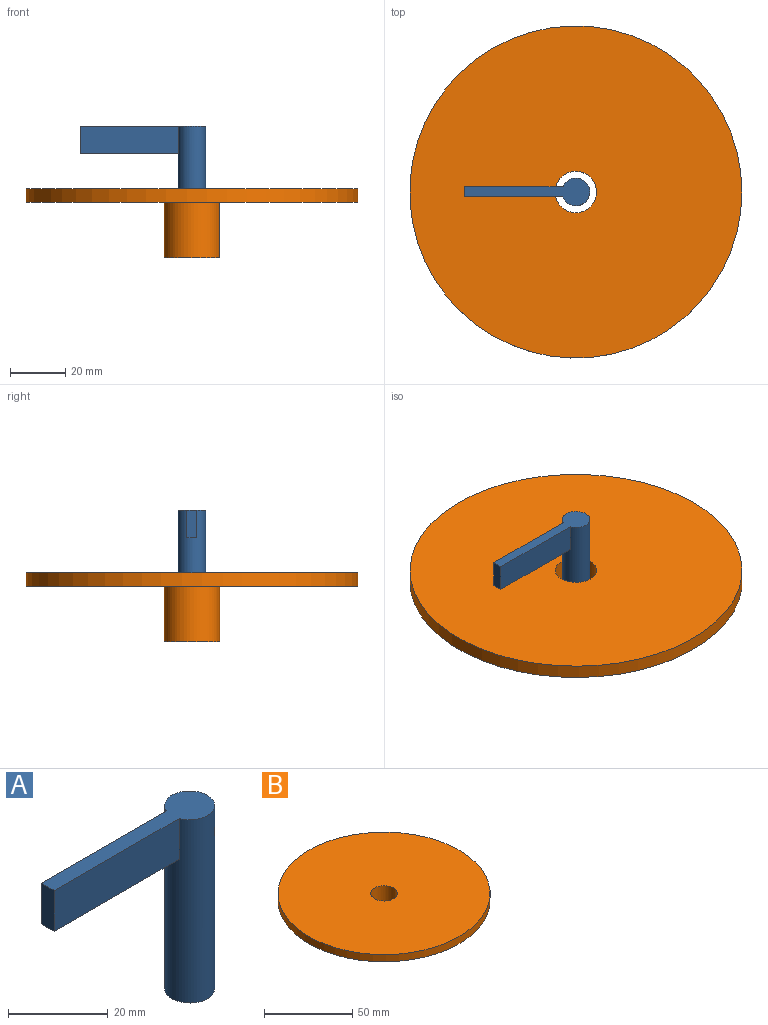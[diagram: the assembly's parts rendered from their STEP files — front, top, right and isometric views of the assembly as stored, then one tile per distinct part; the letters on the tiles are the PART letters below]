
ASSEMBLY  parts=2 mates=1
PART A: 7 faces, bbox 45.1x10x45 mm
  f0: cylinder r=5mm len=45mm, axis (0,0,-1), area 1376.7mm2, adj f1,f2,f3,f4,f6
  f1: plane 45.14x10mm, normal (0,0,1), area 205.9mm2, adj f0,f3,f4,f5
  f2: plane 10x10mm, normal (0,0,-1), area 78.5mm2, adj f0
  f3: plane 35.44x10mm, normal (0,-1,0), area 354.4mm2, adj f0,f1,f5,f6
  f4: plane 35.51x10mm, normal (0,1,0), area 355.1mm2, adj f0,f1,f5,f6
  f5: plane 10x3.61mm, normal (-1,0,0), area 36.1mm2, adj f1,f3,f4,f6
  f6: plane 35.51x3.61mm, normal (0,0,-1), area 127.3mm2, adj f0,f3,f4,f5
PART B: 6 faces, bbox 120x120x25 mm
  f0: cylinder r=7.5mm len=25mm, axis (0,0,-1), area 1178.1mm2, adj f2,f5
  f1: cylinder r=60mm len=120mm, axis (0,0,-1), area 1885mm2, adj f2,f3
  f2: plane 120x120mm, normal (0,0,1), area 11133mm2, adj f0,f1
  f3: plane 120x120mm, normal (0,0,-1), area 10995.6mm2, adj f1,f4
  f4: cylinder r=10mm len=20mm, axis (0,0,1), area 1256.6mm2, adj f3,f5
  f5: plane 20x20mm, normal (0,0,-1), area 137.4mm2, adj f0,f4
PLACE A t=(-18.45,-15.95,-15.23)mm
PLACE B t=(-18.45,-15.95,2.27)mm
MATE cylindrical A.f0 <-> B.f0  axis (0,0,-1) through (-18.45,-15.95,7.27)mm
